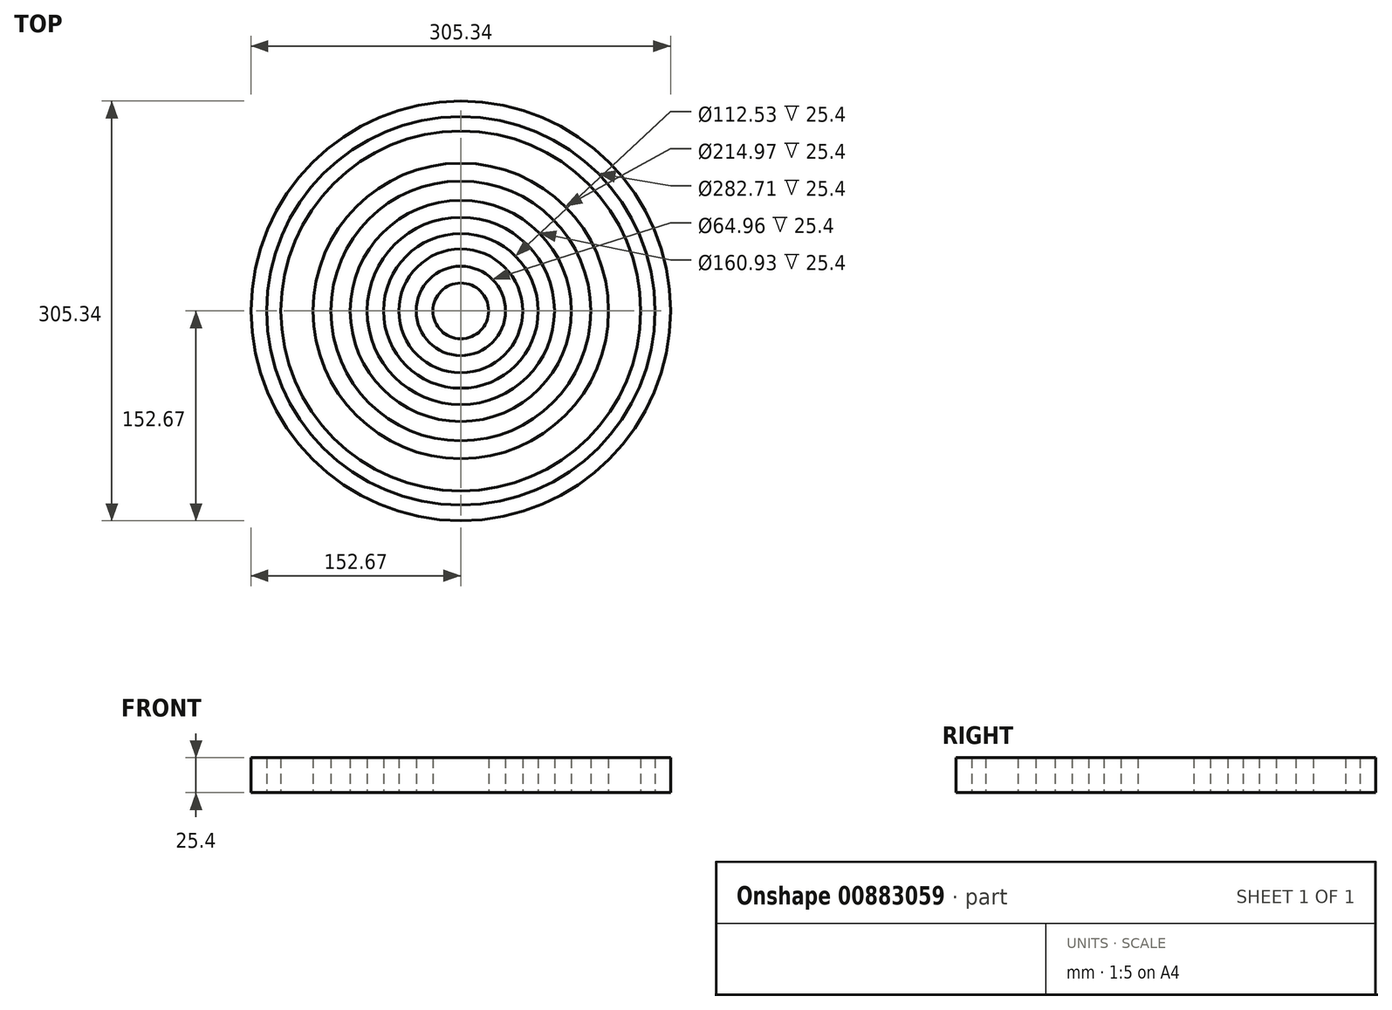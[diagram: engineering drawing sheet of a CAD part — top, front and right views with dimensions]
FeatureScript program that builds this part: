
annotation { "Feature Type Name" : "Feature", "Feature Type Description" : "" }
export const myFeature = defineFeature(function(context is Context, id is Id, definition is map)
    precondition{}
    {
        {
            var Q0;
            Q0=qCreatedBy(makeId("Top.planeOp"),FACE);
            var sketch = newSketch(context, id + "F0", { "sketchPlane" : qUnion([Q0])});
            skCircle(sketch, "E0", {"center": v(0, 0) * mm, "radius": 152.67 * mm});
            skCircle(sketch, "E1", {"center": v(0, 0) * mm, "radius": 141.36 * mm});
            skCircle(sketch, "E2", {"center": v(0, 0) * mm, "radius": 130.96 * mm});
            skCircle(sketch, "E3", {"center": v(0, 0) * mm, "radius": 119.18 * mm});
            skCircle(sketch, "E4", {"center": v(0, 0) * mm, "radius": 107.49 * mm});
            skCircle(sketch, "E5", {"center": v(0, 0) * mm, "radius": 94.53 * mm});
            skCircle(sketch, "E6", {"center": v(0, 0) * mm, "radius": 80.46 * mm});
            skCircle(sketch, "E7", {"center": v(0, 0) * mm, "radius": 68.16 * mm});
            skCircle(sketch, "E8", {"center": v(0, 0) * mm, "radius": 56.26 * mm});
            skCircle(sketch, "E9", {"center": v(0, 0) * mm, "radius": 45.06 * mm});
            skCircle(sketch, "E10", {"center": v(0, 0) * mm, "radius": 32.48 * mm});
            skCircle(sketch, "E11", {"center": v(0, 0) * mm, "radius": 20.29 * mm});
            skCircle(sketch, "E12", {"center": v(0, 0) * mm, "radius": 14.45 * mm});
            skCircle(sketch, "E13", {"center": v(0, 0) * mm, "radius": 9.08 * mm});
            skCircle(sketch, "E14", {"center": v(0, 0) * mm, "radius": 4.95 * mm});
            skSolve(sketch);
        }
        {
            var Q0;
            Q0 = qSketchRegion(id + "F0", true);
            var Q1;
            Q1=makeQuery(id+"F0.imprint","IMPRINT",FACE,{"disambiguationData":[TD([[makeQuery(id+"F0.imprint","IMPRINT",EDGE,{"derivedFrom":sQuery(id+"F0.wireOp",EDGE,"E14")}),1.0]])]});
            var Q2;
            Q2=makeQuery(id+"F0.imprint","IMPRINT",FACE,{"disambiguationData":[TD([[makeQuery(id+"F0.imprint","IMPRINT",EDGE,{"derivedFrom":sQuery(id+"F0.wireOp",EDGE,"E13")}),1.0]])]});
            var Q3;
            Q3=makeQuery(id+"F0.imprint","IMPRINT",FACE,{"disambiguationData":[TD([[makeQuery(id+"F0.imprint","IMPRINT",EDGE,{"derivedFrom":sQuery(id+"F0.wireOp",EDGE,"E12")}),1.0]])]});
            var Q4;
            Q4=makeQuery(id+"F0.imprint","IMPRINT",FACE,{"disambiguationData":[TD([[makeQuery(id+"F0.imprint","IMPRINT",EDGE,{"derivedFrom":sQuery(id+"F0.wireOp",EDGE,"E11")}),1.0]])]});
            var Q5;
            Q5=makeQuery(id+"F0.imprint","IMPRINT",FACE,{"disambiguationData":[TD([[makeQuery(id+"F0.imprint","IMPRINT",EDGE,{"derivedFrom":sQuery(id+"F0.wireOp",EDGE,"E9")}),1.0]])]});
            var Q6;
            Q6=makeQuery(id+"F0.imprint","IMPRINT",FACE,{"disambiguationData":[TD([[makeQuery(id+"F0.imprint","IMPRINT",EDGE,{"derivedFrom":sQuery(id+"F0.wireOp",EDGE,"E7")}),1.0]])]});
            var Q7;
            Q7=makeQuery(id+"F0.imprint","IMPRINT",FACE,{"disambiguationData":[TD([[makeQuery(id+"F0.imprint","IMPRINT",EDGE,{"derivedFrom":sQuery(id+"F0.wireOp",EDGE,"E5")}),1.0]])]});
            var Q8;
            Q8=makeQuery(id+"F0.imprint","IMPRINT",FACE,{"disambiguationData":[TD([[makeQuery(id+"F0.imprint","IMPRINT",EDGE,{"derivedFrom":sQuery(id+"F0.wireOp",EDGE,"E3")}),1.0]])]});
            var Q9;
            Q9=makeQuery(id+"F0.imprint","IMPRINT",FACE,{"disambiguationData":[TD([[makeQuery(id+"F0.imprint","IMPRINT",EDGE,{"derivedFrom":sQuery(id+"F0.wireOp",EDGE,"E2")}),1.0]])]});
            extrude(context, id + "F1", {"entities" : qUnion([Q0, Q1, Q2, Q3, Q4, Q5, Q6, Q7, Q8, Q9]), "depth" : 25.4 * mm, "offsetDistance" : 25.4 * mm});
        }
    });
